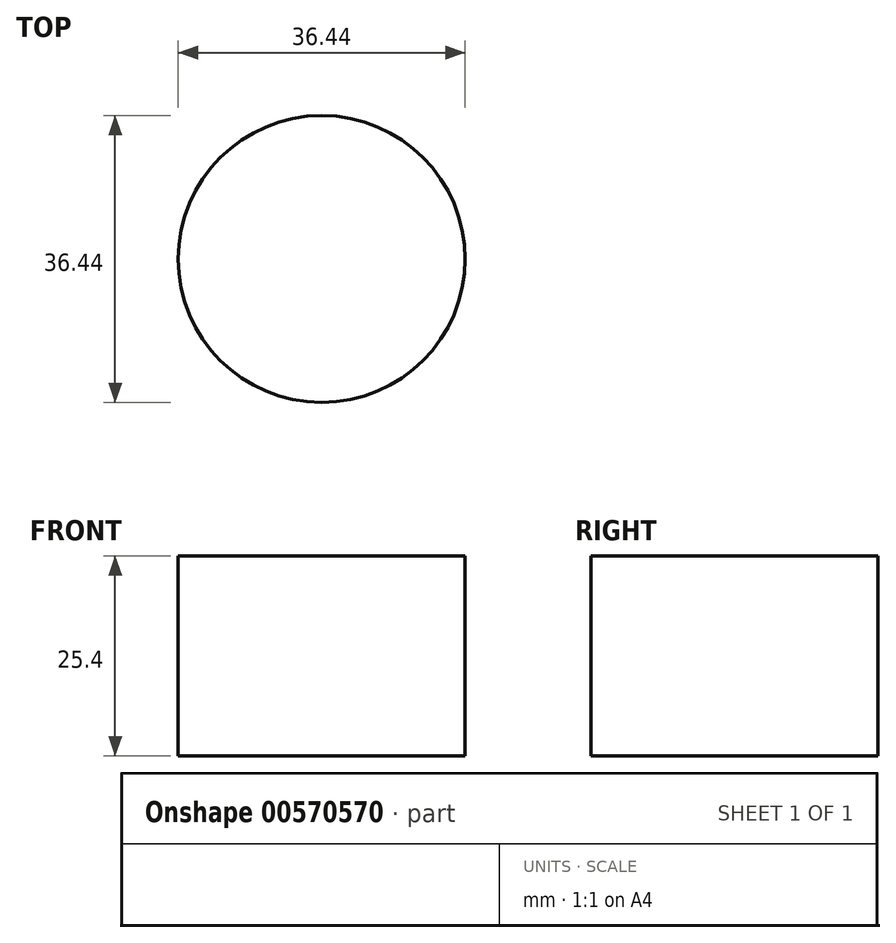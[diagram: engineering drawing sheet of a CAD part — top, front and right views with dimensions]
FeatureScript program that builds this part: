
annotation { "Feature Type Name" : "Feature", "Feature Type Description" : "" }
export const myFeature = defineFeature(function(context is Context, id is Id, definition is map)
    precondition{}
    {
        {
            var Q0;
            Q0=qCreatedBy(makeId("Top.planeOp"),FACE);
            var sketch = newSketch(context, id + "F0", { "sketchPlane" : qUnion([Q0])});
            skCircle(sketch, "E0", {"center": v(0, 0) * mm, "radius": 21.56 * mm});
            skCircle(sketch, "E1", {"center": v(0, 0) * mm, "radius": 18.22 * mm});
            skSolve(sketch);
        }
        {
            var Q0;
            Q0=sQuery(id+"F0.wireOp",EDGE,"E1");
            extrude(context, id + "F1", {"bodyType" : ToolBodyType.SURFACE, "surfaceEntities" : qUnion([Q0]), "depth" : 25.4 * mm, "offsetDistance" : 25.4 * mm});
        }
    });
